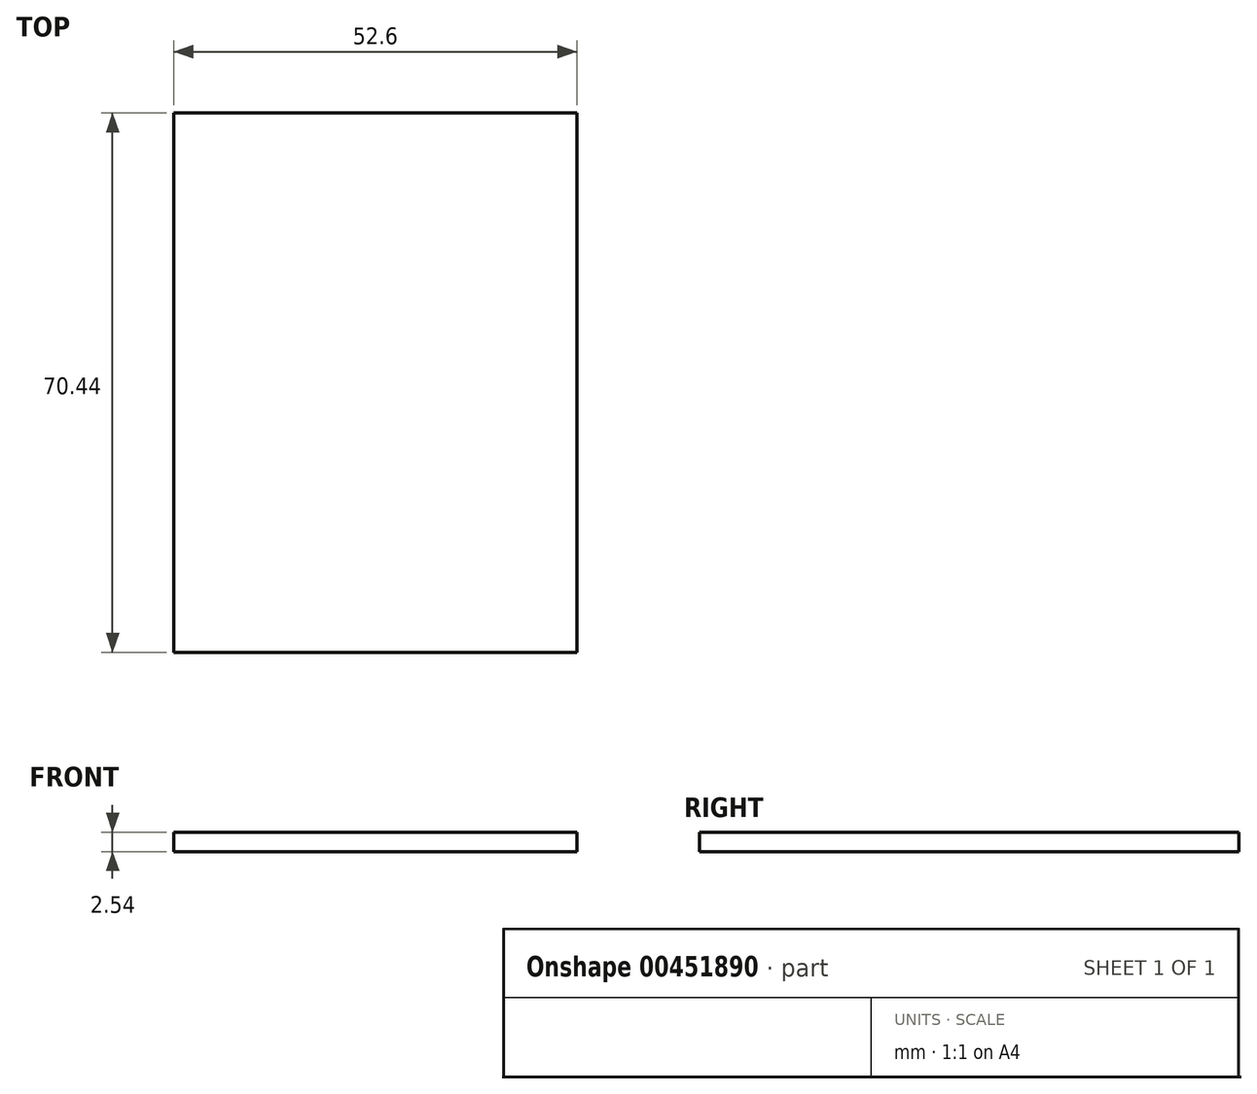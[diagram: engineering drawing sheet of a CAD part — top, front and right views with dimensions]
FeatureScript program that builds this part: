
annotation { "Feature Type Name" : "Feature", "Feature Type Description" : "" }
export const myFeature = defineFeature(function(context is Context, id is Id, definition is map)
    precondition{}
    {
        {
            var Q0;
            Q0=qCreatedBy(makeId("Front.planeOp"),FACE);
            var sketch = newSketch(context, id + "F0", { "sketchPlane" : qUnion([Q0])});
            skCircle(sketch, "E0", {"center": v(0, 0) * mm, "radius": 11.94 * mm});
            skSolve(sketch);
        }
        {
            var Q0;
            Q0 = qSketchRegion(id + "F0", true);
            extrude(context, id + "F1", {"entities" : qUnion([Q0]), "depth" : 14.48 * mm});
        }
        {
            var Q0;
            Q0=makeQuery(id+"F1.opExtrude","SWEPT_BODY",BODY,{"disambiguationData":[OSD([sQuery(id+"F0.wireOp",EDGE,"E0")])]});
            deleteBodies(context, id + "F2", {"entities" : qUnion([Q0])});
        }
        {
            var Q0;
            Q0=qCreatedBy(makeId("Front.planeOp"),FACE);
            var sketch = newSketch(context, id + "F3", { "sketchPlane" : qUnion([Q0])});
            skLineSegment(sketch, "E1.bottom", {"start": v(-47.6, 29.63) * mm, "end": v(47.6, 29.63) * mm});
            skLineSegment(sketch, "E1.top", {"start": v(-47.6, -29.63) * mm, "end": v(47.6, -29.63) * mm});
            skLineSegment(sketch, "E1.left", {"start": v(-47.6, 29.63) * mm, "end": v(-47.6, -29.63) * mm});
            skLineSegment(sketch, "E1.right", {"start": v(47.6, 29.63) * mm, "end": v(47.6, -29.63) * mm});
            skPoint(sketch, "E1.middle", {"position": v(0, 0) * mm});
            skSolve(sketch);
        }
        {
            var Q0;
            Q0=makeQuery(id+"F3.imprint","IMPRINT",FACE,{"disambiguationData":[TD([[makeQuery(id+"F3.imprint","IMPRINT",EDGE,{"derivedFrom":sQuery(id+"F3.wireOp",EDGE,"E1.bottom")}),-1.0]])]});
            extrude(context, id + "F4", {"entities" : qUnion([Q0]), "depth" : 25.4 * mm, "hasSecondDirection" : true, "secondDirectionOppositeDirection" : true, "secondDirectionDepth" : 25.4 * mm});
        }
        {
            var Q0;
            Q0=makeQuery(id+"F4.opExtrude","SWEPT_BODY",BODY,{"disambiguationData":[OSD([sQuery(id+"F3.wireOp",EDGE,"E1.bottom"),sQuery(id+"F3.wireOp",EDGE,"E1.top"),sQuery(id+"F3.wireOp",EDGE,"E1.left"),sQuery(id+"F3.wireOp",EDGE,"E1.right")])]});
            deleteBodies(context, id + "F5", {"entities" : qUnion([Q0])});
        }
        {
            var Q0;
            Q0=qCreatedBy(makeId("Top.planeOp"),FACE);
            var sketch = newSketch(context, id + "F6", { "sketchPlane" : qUnion([Q0])});
            skLineSegment(sketch, "E2.bottom", {"start": v(-26.3, 35.22) * mm, "end": v(26.3, 35.22) * mm});
            skLineSegment(sketch, "E2.top", {"start": v(-26.3, -35.22) * mm, "end": v(26.3, -35.22) * mm});
            skLineSegment(sketch, "E2.left", {"start": v(-26.3, 35.22) * mm, "end": v(-26.3, -35.22) * mm});
            skLineSegment(sketch, "E2.right", {"start": v(26.3, 35.22) * mm, "end": v(26.3, -35.22) * mm});
            skPoint(sketch, "E2.middle", {"position": v(0, 0) * mm});
            skSolve(sketch);
        }
        {
            var Q0;
            Q0=makeQuery(id+"F6.imprint","IMPRINT",FACE,{"disambiguationData":[TD([[makeQuery(id+"F6.imprint","IMPRINT",EDGE,{"derivedFrom":sQuery(id+"F6.wireOp",EDGE,"E2.bottom")}),-1.0]])]});
            extrude(context, id + "F7", {"entities" : qUnion([Q0]), "depth" : 2.54 * mm});
        }
    });
